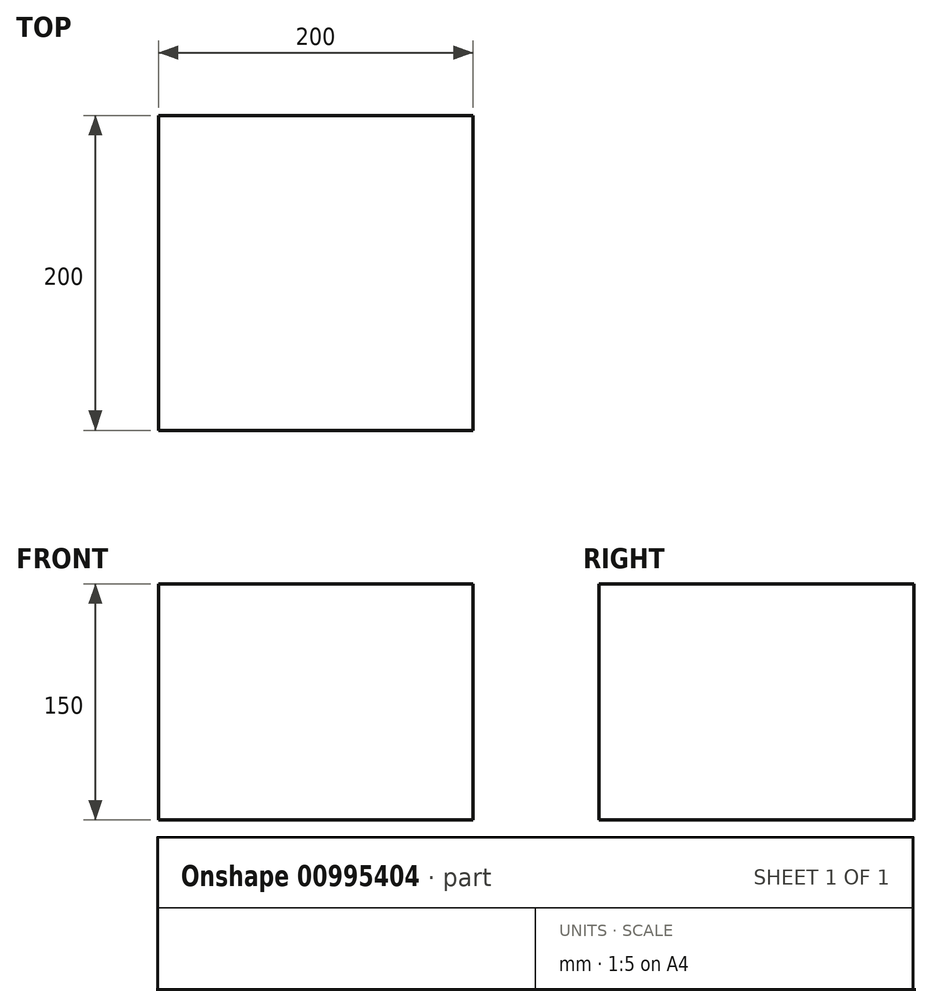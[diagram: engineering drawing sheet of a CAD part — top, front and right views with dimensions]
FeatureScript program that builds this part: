
annotation { "Feature Type Name" : "Feature", "Feature Type Description" : "" }
export const myFeature = defineFeature(function(context is Context, id is Id, definition is map)
    precondition{}
    {
        {
            var Q0;
            Q0=qCreatedBy(makeId("Front.planeOp"),FACE);
            var sketch = newSketch(context, id + "F0", { "sketchPlane" : qUnion([Q0])});
            skLineSegment(sketch, "E0", {"start": v(0, 0) * mm, "end": v(200, 0) * mm});
            skLineSegment(sketch, "E1", {"start": v(200, 0) * mm, "end": v(200, 150) * mm});
            skLineSegment(sketch, "E2", {"start": v(200, 150) * mm, "end": v(0, 150) * mm});
            skLineSegment(sketch, "E3", {"start": v(0, 150) * mm, "end": v(0, 0) * mm});
            skSolve(sketch);
        }
        {
            var Q0;
            Q0 = qSketchRegion(id + "F0", true);
            extrude(context, id + "F1", {"entities" : qUnion([Q0]), "depth" : 200 * mm, "offsetDistance" : 25 * mm});
        }
    });
